# Revit family: DOME-S-KG 14800-840 MPS-DA
name_source: partatom
category: Oprawy oświetleniowe
revit_build: Autodesk Revit 2017 (Build: 20190508_0315(x64)
units: mm (PartAtom-declared; Revit-internal decimal feet)

## family parameters
Numer OmniClass = 23.80.70.11
Obiekt nadrzędny = Powierzchnia
Punkt obliczania pomieszczeń = Nie
Tnij formami wycięć po wczytaniu = Nie
Typ części = Normalny
Tytuł OmniClass = Luminaries for Internal Lighting
Współdzielony = Nie
Wymiar okrągłego złącza = Użyj średnicy
Źródło światła = Tak

## types (1)
- DOME-S-KG 14800-840 MPS-DA
    Domyślna rzędna = 0 mm  [stored 0 ft]
    Emituj kształt widoczny w renderingu = Nie
    Emituj z długości prostokąta = 251 mm  [stored 0.823491 ft]
    Emituj z szerokości prostokąta = 581 mm  [stored 1.90617 ft]
    Filtr koloru = 16777215
    Kod zespołu = D5020200
    Lampa = LED
    Model = SPG0630173
    Obciążenie pozorne = 90 VA
    Odchylenie kierunku = 90.00°
    Plik sieci fotometrycznej = DOME-S-KG 14800-840 MPS-DA.IES
    Producent = RIDI Leuchten GmbH
    URL = https://www.spectral-lighting.com
    Zmiana temperatury barwowej przyciemniania lampy = <Brak>
    brand = Spectral
    conformity mark = CE
    electrical safety class = 1
    height = 1945 mm  [stored 6.38123 ft]
    ingress protection (IP) code = IP20
    length = 742 mm  [stored 2.43438 ft]
    nominal frequency = 50-60Hz
    nominal voltage = 230
    product name = DOME-S-KG 14800-840 MPS-DA
    rated input power = 90
    voltage type (AC, DC, UC) = AC
    weight = 27.2 kg
    width = 450 mm  [stored 1.47638 ft]

note: [stored X ft] marks values corroborated as IEEE doubles in the binary element streams (Revit-internal decimal feet)
